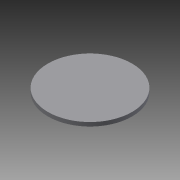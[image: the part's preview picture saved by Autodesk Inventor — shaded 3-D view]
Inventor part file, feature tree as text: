
AUTODESK INVENTOR PART (.ipt)
format: ipt  version: 2015 (Build 190159000, 159)  size: 67,584 bytes
history: native  units: in
note: dims shown in document units (in); Inventor stores cm internally (conversion verified against a paired STEP export)
features: extrude x1, sketch x1
ambient origin geometry x8: Origin, YZ Plane, XZ Plane, XY Plane, X Axis, Y Axis, Z Axis, Center Point
bodies: Solid1 (feature_tree)
feature tree (2):
  extrude  "Extrusion1"  Depth=0.15in TaperAngle=0.0deg
  sketch  "Sketch1"  dims[d0=3.25in d1=0.15in d2=0.0in]
